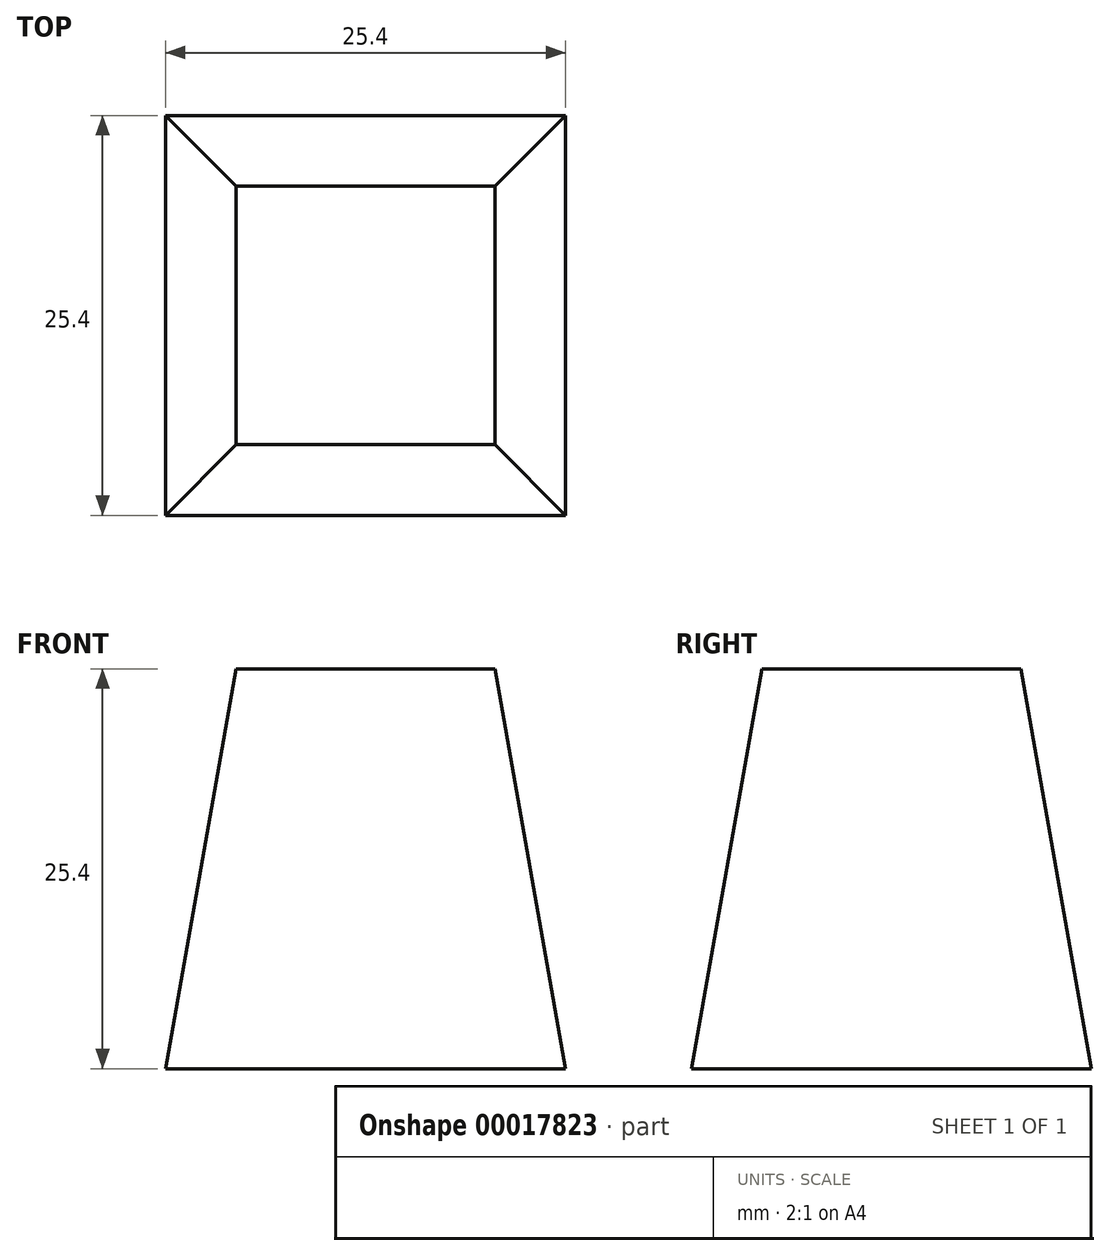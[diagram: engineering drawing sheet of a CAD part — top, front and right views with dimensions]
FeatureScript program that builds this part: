
annotation { "Feature Type Name" : "Feature", "Feature Type Description" : "" }
export const myFeature = defineFeature(function(context is Context, id is Id, definition is map)
    precondition{}
    {
        {
            var Q0;
            Q0=qCreatedBy(makeId("Top.planeOp"),FACE);
            var sketch = newSketch(context, id + "F0", { "sketchPlane" : qUnion([Q0])});
            skLineSegment(sketch, "E0.bottom", {"start": v(0, 0) * mm, "end": v(-25.4, 0) * mm});
            skLineSegment(sketch, "E0.top", {"start": v(0, 25.4) * mm, "end": v(-25.4, 25.4) * mm});
            skLineSegment(sketch, "E0.left", {"start": v(0, 0) * mm, "end": v(0, 25.4) * mm});
            skLineSegment(sketch, "E0.right", {"start": v(-25.4, 0) * mm, "end": v(-25.4, 25.4) * mm});
            skSolve(sketch);
        }
        {
            var Q0;
            Q0 = qSketchRegion(id + "F0", true);
            extrude(context, id + "F1", {"entities" : qUnion([Q0]), "depth" : 25.4 * mm, "hasDraft" : true, "draftAngle" : 10 * degree, "draftPullDirection" : true});
        }
    });
